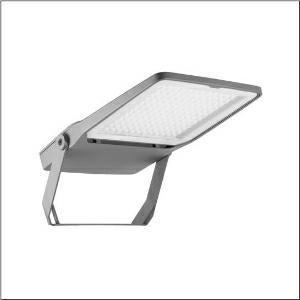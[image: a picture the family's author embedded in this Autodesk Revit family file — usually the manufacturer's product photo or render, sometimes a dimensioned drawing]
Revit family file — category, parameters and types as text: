
# Revit family: floodlight_fl_20_midi___pl43_5xa7682d1a1ac_a646
name_source: partatom
category: Lighting Fixtures
units: mm (PartAtom-declared; Revit-internal decimal feet)

## family parameters
Cut with Voids When Loaded = No
Host = Face
Light Source = No
Part Type = Normal
Room Calculation Point = No
Round Connector Dimension = Use Diameter
Shared = No

## types (1)
- --- (1 x LED 3000K / CRI = 80 (unbekannt), 14980 lm, 3000K)
    Apparent Load = 142 VA
    CIE Flux Codes = 32 74 99 100 100
    Color Rendering = 80
    Color Temperature = 3000K
    Default Elevation = 1800 mm
    Description = Floodlight FL 20 midi, floodlight, primary light control with lens, of plastic, primary optical cover: protective disc, of toughened safety glass, transparent, light distribution: PL43, light emission: direct distribution, primary light characteristic: asymmetric, installation type: surface-mounted, LED High Power LED, rated luminous flux: 14.980 lm, light colour: 830, colour temperature: 3000K, control gear: ECG Plus, control: flexible luminous flux parameterisation, time-dependent luminous flux control, digital communication interface, power reduction, overheat protection, electronic power reduction, with terminal, 5-pole, max. 2.5mm², mains connection: 220..240V, AC, 50/60Hz, rated input power: 142W, LED unit, of diecast aluminium, powder-coated, Siteco® metallic grey (DB 702S), length: 654 mm, width: 450 mm, height: 76mm, housing frame, of diecast aluminium, powder-coated, Siteco® metallic grey (DB 702S), mounting bracket, of steel, powder-coated, Siteco® metallic grey (DB 702S), DALIprotection rating (complete): IP66, insulation class (complete): insulation class II (safety insulation), certification: CE, ENEC, VDE, protection symbol: D, permissible ambient temperature for indoor applications: -40..+40°C, permissible ambient temperature for outdoor applications: -40..+50°C, standard: DIN EN 12944, packaging unit: 1 piece

Light Distribution: PL43
    Height = 76 mm
    Lamp = 1 x LED 3000K / CRI >= 80 (unbekannt)
    Lamp Light Flux = 14980 lm
    Lamp count = 1
    Length = 672 mm
    Luminous efficacy = 105 lm/W
    Manufacturer = Siteco
    ModVariant = No
    Model = 5XA7682D1A1AC
    Number of Poles = 1
    OnlyDefault = Yes
    Power Factor = 1
    Product Name = Floodlight FL 20 midi | PL43
    Product group = floodlight | pylon top
    ProductGroupID = 6101
    Protection Class = Protection class II
    Protection Degree = IP 66
    RLX_Detail_Level = 1
    RlxData = <blob elided: 97505 chars, md5=624371ba>
    Socket = socket
    Standby Power = 0 W
    System Light Flux = 14980 lm
    System Power = 142 W
    Type Comments = factory setting: luminous flux: 100 % | dim-lin: 254 | 489 mA
    Type Image = l_1005943.jpg
    URL = http://relux.com
    VarID = @adj_144093
    Voltage = 0 V
    Weight = 0.00 kg
    Width = 450 mm

## geometry (parser evidence)
native form markers: Blend x4, Sweep x11
no freeform markers — native parametric forms only
